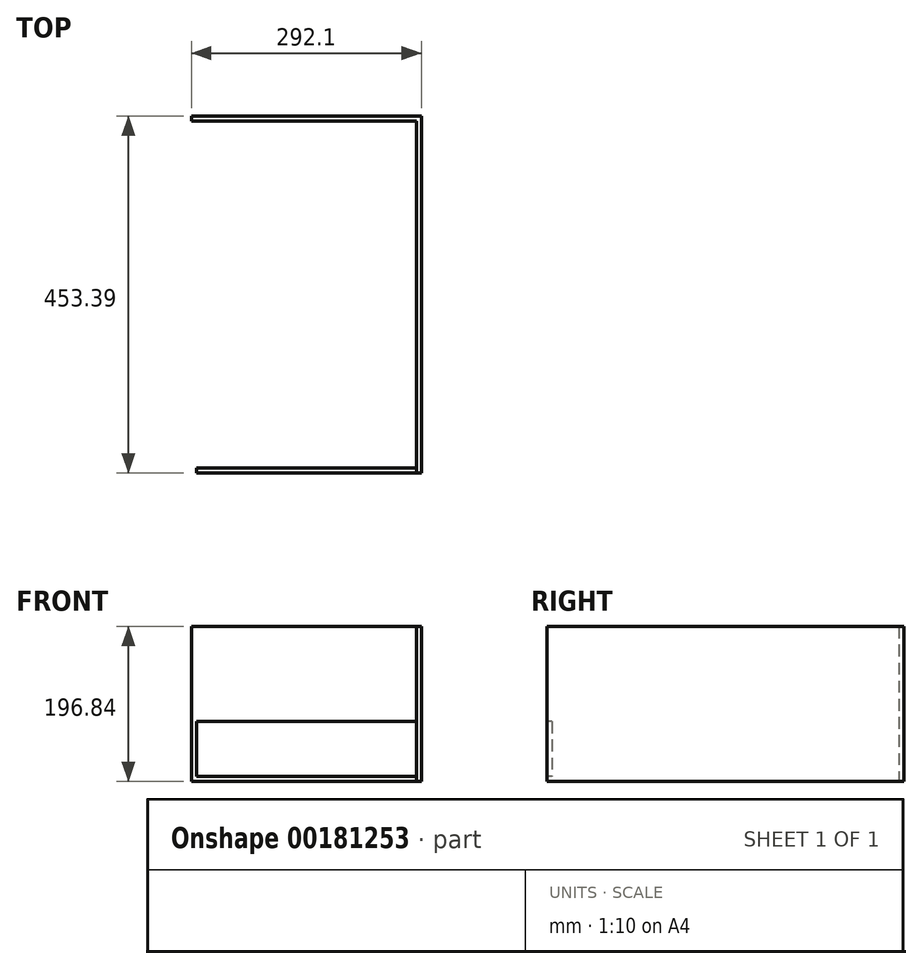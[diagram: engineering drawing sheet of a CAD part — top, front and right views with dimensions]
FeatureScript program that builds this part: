
annotation { "Feature Type Name" : "Feature", "Feature Type Description" : "" }
export const myFeature = defineFeature(function(context is Context, id is Id, definition is map)
    precondition{}
    {
        {
            var Q0;
            Q0=qCreatedBy(makeId("Front.planeOp"),FACE);
            var sketch = newSketch(context, id + "F0", { "sketchPlane" : qUnion([Q0])});
            skLineSegment(sketch, "E0.bottom", {"start": v(146.05, 98.43) * mm, "end": v(139.7, 98.43) * mm});
            skLineSegment(sketch, "E0.top", {"start": v(146.05, -98.43) * mm, "end": v(-146.05, -98.43) * mm});
            skLineSegment(sketch, "E0.left", {"start": v(146.05, 98.42) * mm, "end": v(146.05, -98.43) * mm});
            skLineSegment(sketch, "E0.right", {"start": v(-146.05, 98.43) * mm, "end": v(-146.05, -98.43) * mm});
            skPoint(sketch, "E0.middle", {"position": v(0, 0) * mm});
            skLineSegment(sketch, "E1.bottom", {"start": v(-146.05, 98.43) * mm, "end": v(-139.7, 98.43) * mm});
            skLineSegment(sketch, "E1.top", {"start": v(-146.05, -98.43) * mm, "end": v(-139.7, -98.43) * mm});
            skLineSegment(sketch, "E1.right", {"start": v(-139.7, 98.43) * mm, "end": v(-139.7, -98.43) * mm});
            skLineSegment(sketch, "E2.top", {"start": v(146.05, -98.43) * mm, "end": v(139.7, -98.43) * mm});
            skLineSegment(sketch, "E2.left", {"start": v(146.05, 98.43) * mm, "end": v(146.05, -98.43) * mm});
            skLineSegment(sketch, "E2.right", {"start": v(139.7, 98.43) * mm, "end": v(139.7, -98.43) * mm});
            skLineSegment(sketch, "E3.bottom", {"start": v(-139.7, -98.43) * mm, "end": v(139.7, -98.43) * mm});
            skLineSegment(sketch, "E3.top", {"start": v(-139.7, -22.23) * mm, "end": v(139.7, -22.23) * mm});
            skLineSegment(sketch, "E3.left", {"start": v(-139.7, -98.43) * mm, "end": v(-139.7, -22.23) * mm});
            skLineSegment(sketch, "E3.right", {"start": v(139.7, -98.43) * mm, "end": v(139.7, -22.23) * mm});
            skLineSegment(sketch, "E4.trimOffspring", {"start": v(-139.7, 98.43) * mm, "end": v(-146.05, 98.43) * mm});
            skLineSegment(sketch, "E5.top", {"start": v(-139.7, -92.08) * mm, "end": v(139.7, -92.08) * mm});
            skLineSegment(sketch, "E5.left", {"start": v(-139.7, -98.43) * mm, "end": v(-139.7, -92.08) * mm});
            skLineSegment(sketch, "E5.right", {"start": v(139.7, -98.43) * mm, "end": v(139.7, -92.08) * mm});
            skLineSegment(sketch, "E6.bottom", {"start": v(88.9, -92.08) * mm, "end": v(-88.9, -92.08) * mm});
            skLineSegment(sketch, "E6.left", {"start": v(88.9, -92.08) * mm, "end": v(88.9, -98.43) * mm});
            skLineSegment(sketch, "E6.right", {"start": v(-88.9, -92.08) * mm, "end": v(-88.9, -98.43) * mm});
            skPoint(sketch, "E6.middle", {"position": v(0, -98.43) * mm});
            skPoint(sketch, "E6.top.end.orphan", {"position": v(-88.9, -104.78) * mm});
            skPoint(sketch, "E7.orphan", {"position": v(88.9, -104.77) * mm});
            skSolve(sketch);
        }
        {
            var Q0;
            Q0=makeQuery(id+"F0.imprint","IMPRINT",FACE,{"disambiguationData":[TD([[makeQuery(id+"F0.imprint","IMPRINT",EDGE,{"derivedFrom":sQuery(id+"F0.wireOp",EDGE,"E1.top")}),1.0]])]});
            var Q1;
            {var subQ0=sQuery(id+"F0.wireOp",EDGE,"E5.left");Q1=makeQuery(id+"F0.imprint","IMPRINT",FACE,{"disambiguationData":[TD([[makeQuery(id+"F0.imprint","IMPRINT",EDGE,{"derivedFrom":subQ0}),-1.0]])]});}
            var Q2;
            {var subQ0=sQuery(id+"F0.wireOp",EDGE,"E5.right");Q2=makeQuery(id+"F0.imprint","IMPRINT",FACE,{"disambiguationData":[TD([[makeQuery(id+"F0.imprint","IMPRINT",EDGE,{"derivedFrom":subQ0}),1.0]])]});}
            var Q3;
            Q3=makeQuery(id+"F0.imprint","IMPRINT",FACE,{"disambiguationData":[TD([[makeQuery(id+"F0.imprint","IMPRINT",EDGE,{"derivedFrom":sQuery(id+"F0.wireOp",EDGE,"E0.bottom")}),1.0]])]});
            var Q4;
            Q4=makeQuery(id+"F0.imprint","IMPRINT",FACE,{"disambiguationData":[TD([[makeQuery(id+"F0.imprint","IMPRINT",EDGE,{"derivedFrom":sQuery(id+"F0.wireOp",EDGE,"E6.bottom")}),1.0]])]});
            extrude(context, id + "F1", {"entities" : qUnion([Q0, Q1, Q2, Q3, Q4]), "oppositeDirection" : true, "depth" : 453.4 * mm});
        }
        {
            var Q0;
            Q0=makeQuery(id+"F0.imprint","IMPRINT",FACE,{"disambiguationData":[TD([[makeQuery(id+"F0.imprint","IMPRINT",EDGE,{"derivedFrom":sQuery(id+"F0.wireOp",EDGE,"E3.top")}),-1.0]])]});
            var Q1;
            Q1=makeQuery(id+"F0.imprint","IMPRINT",FACE,{"disambiguationData":[TD([[makeQuery(id+"F0.imprint","IMPRINT",EDGE,{"derivedFrom":sQuery(id+"F0.wireOp",EDGE,"E6.bottom")}),1.0]])]});
            var Q2;
            {var subQ0=sQuery(id+"F0.wireOp",EDGE,"E5.left");Q2=makeQuery(id+"F0.imprint","IMPRINT",FACE,{"disambiguationData":[TD([[makeQuery(id+"F0.imprint","IMPRINT",EDGE,{"derivedFrom":subQ0}),-1.0]])]});}
            var Q3;
            {var subQ0=sQuery(id+"F0.wireOp",EDGE,"E5.right");Q3=makeQuery(id+"F0.imprint","IMPRINT",FACE,{"disambiguationData":[TD([[makeQuery(id+"F0.imprint","IMPRINT",EDGE,{"derivedFrom":subQ0}),1.0]])]});}
            extrude(context, id + "F2", {"entities" : qUnion([Q0, Q1, Q2, Q3]), "oppositeDirection" : true, "depth" : 6.35 * mm});
        }
        {
            var Q0;
            Q0=makeQuery(id+"F1.opExtrude","CAP_FACE",FACE,{"disambiguationData":[OSD([sQuery(id+"F0.wireOp",EDGE,"E0.bottom"),sQuery(id+"F0.wireOp",EDGE,"E2.top"),sQuery(id+"F0.wireOp",EDGE,"E2.left"),sQuery(id+"F0.wireOp",EDGE,"E2.right"),sQuery(id+"F0.wireOp",EDGE,"E3.right"),sQuery(id+"F0.wireOp",EDGE,"E3.bottom"),sQuery(id+"F0.wireOp",EDGE,"E5.top"),sQuery(id+"F0.wireOp",EDGE,"E6.left")])],"isStart":false});
            var sketch = newSketch(context, id + "F3", { "sketchPlane" : qUnion([Q0])});
            skLineSegment(sketch, "E8.bottom", {"start": v(-146.05, -98.43) * mm, "end": v(146.05, -98.43) * mm});
            skLineSegment(sketch, "E8.top", {"start": v(-146.05, 98.43) * mm, "end": v(146.05, 98.43) * mm});
            skLineSegment(sketch, "E8.left", {"start": v(-146.05, -98.43) * mm, "end": v(-146.05, 98.43) * mm});
            skLineSegment(sketch, "E8.right", {"start": v(146.05, -98.43) * mm, "end": v(146.05, 98.43) * mm});
            skSolve(sketch);
        }
        {
            var Q0;
            Q0 = qSketchRegion(id + "F3", true);
            extrude(context, id + "F4", {"entities" : qUnion([Q0]), "operationType" : NewBodyOperationType.ADD, "oppositeDirection" : true, "depth" : 6.35 * mm});
        }
    });
